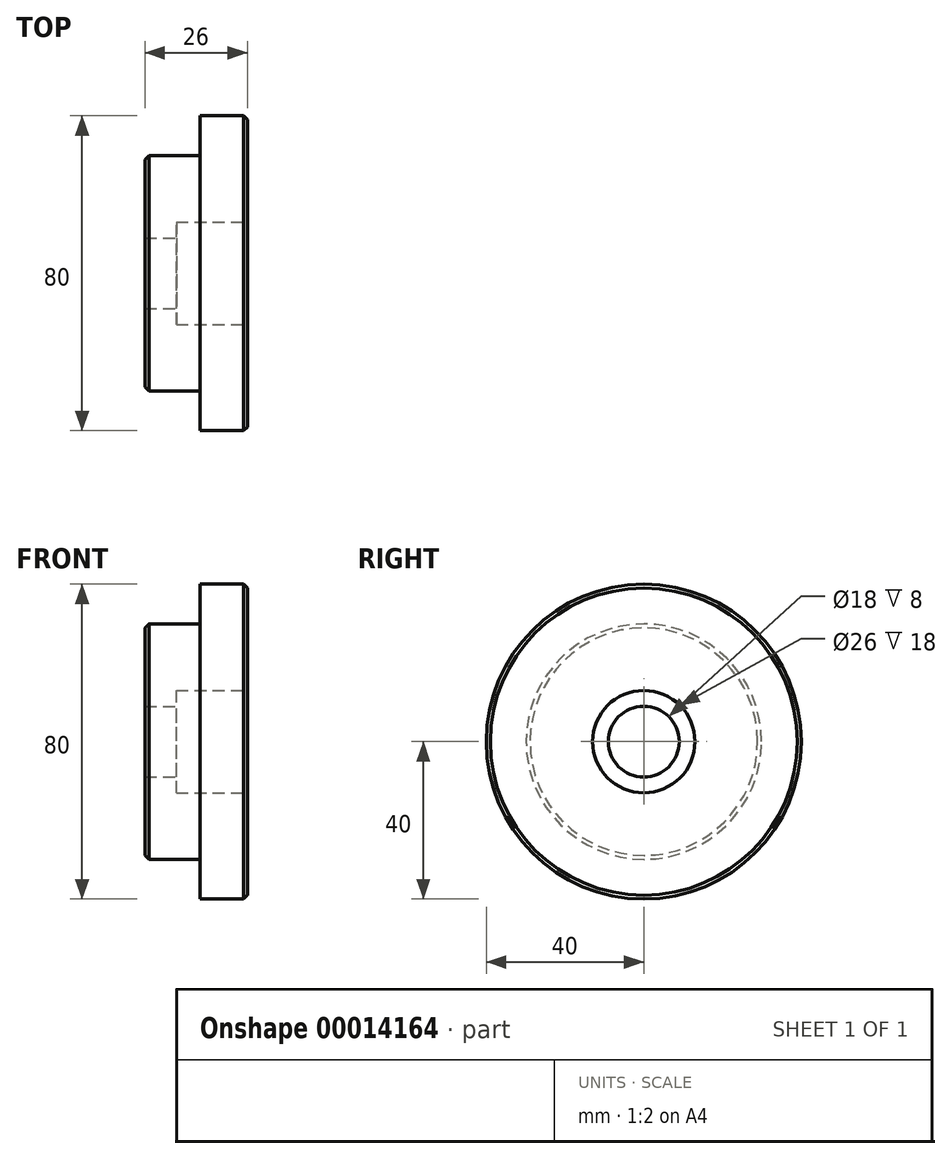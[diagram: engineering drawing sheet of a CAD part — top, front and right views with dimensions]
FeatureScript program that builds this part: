
annotation { "Feature Type Name" : "Feature", "Feature Type Description" : "" }
export const myFeature = defineFeature(function(context is Context, id is Id, definition is map)
    precondition{}
    {
        {
            var Q0;
            Q0=qCreatedBy(makeId("Right.planeOp"),FACE);
            var sketch = newSketch(context, id + "F0", { "sketchPlane" : qUnion([Q0])});
            skCircle(sketch, "E0", {"center": v(0, 0) * mm, "radius": 40 * mm});
            skSolve(sketch);
        }
        {
            var Q0;
            Q0 = qSketchRegion(id + "F0", true);
            extrude(context, id + "F1", {"entities" : qUnion([Q0]), "depth" : 12 * mm});
        }
        {
            var Q0;
            Q0=makeQuery(id+"F1.opExtrude","CAP_FACE",FACE,{"disambiguationData":[OSD([sQuery(id+"F0.wireOp",EDGE,"E0")])],"isStart":true});
            var sketch = newSketch(context, id + "F2", { "sketchPlane" : qUnion([Q0])});
            skCircle(sketch, "E1", {"center": v(0, 0) * mm, "radius": 29.9 * mm});
            skSolve(sketch);
        }
        {
            var Q0;
            Q0 = qSketchRegion(id + "F2", true);
            extrude(context, id + "F3", {"entities" : qUnion([Q0]), "operationType" : NewBodyOperationType.ADD, "depth" : 14 * mm});
        }
        {
            var Q0;
            Q0=makeQuery(id+"F3.opExtrude","CAP_EDGE",EDGE,{"disambiguationData":[OSD([sQuery(id+"F2.wireOp",EDGE,"E1")])],"isStart":false});
            var Q1;
            Q1=makeQuery(id+"F1.opExtrude","CAP_EDGE",EDGE,{"disambiguationData":[OSD([sQuery(id+"F0.wireOp",EDGE,"E0")])],"isStart":false});
            chamfer(context, id + "F4", {"entities" : qUnion([Q0, Q1]), "width" : 1 * mm, "tangentPropagation" : true});
        }
        {
            var Q0;
            Q0=makeQuery(id+"F1.opExtrude","CAP_FACE",FACE,{"disambiguationData":[OSD([sQuery(id+"F0.wireOp",EDGE,"E0")])],"isStart":false});
            var sketch = newSketch(context, id + "F5", { "sketchPlane" : qUnion([Q0])});
            skLineSegment(sketch, "E2", {"start": v(0, 0) * mm, "end": v(-51.58, 0) * mm, "construction": true});
            skSolve(sketch);
        }
        {
            var Q0;
            Q0=sQuery(id+"F5.wireOp",VERTEX,"E2.start");
            var Q1;
            Q1=makeQuery(id+"F1.opExtrude","SWEPT_BODY",BODY,{"disambiguationData":[OSD([sQuery(id+"F0.wireOp",EDGE,"E0")])]});
            hole(context, id + "F6", {"style" : HoleStyle.C_BORE, "holeDiameter" : 18 * mm, "cBoreDiameter" : 26 * mm, "cBoreDepth" : 18 * mm, "endStyle" : HoleEndStyle.THROUGH, "locations" : qUnion([Q0]), "scope" : qUnion([Q1])});
        }
    });
